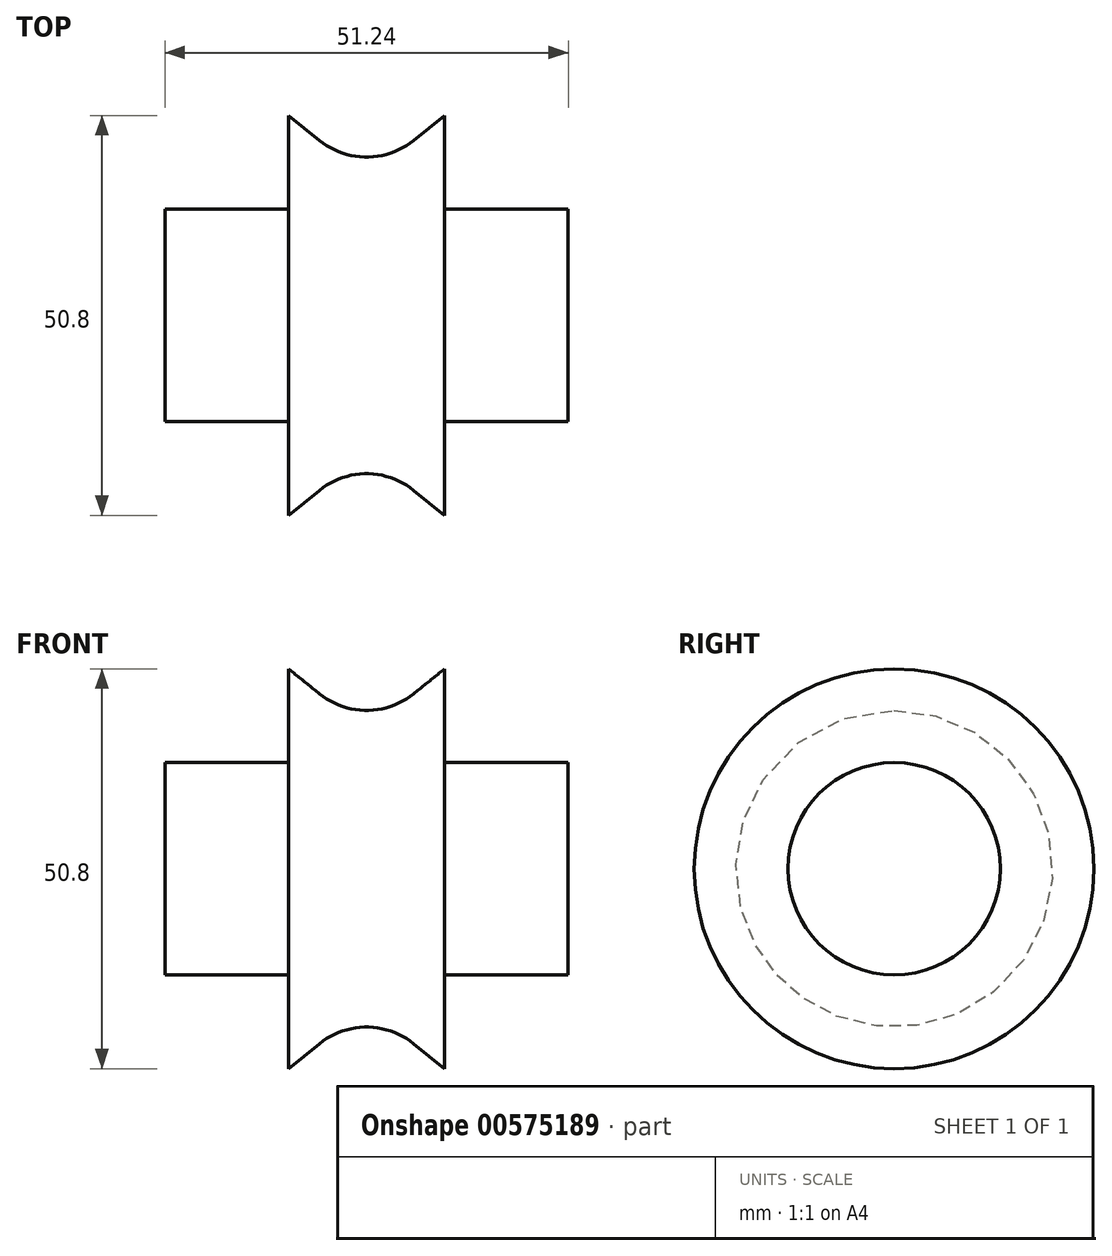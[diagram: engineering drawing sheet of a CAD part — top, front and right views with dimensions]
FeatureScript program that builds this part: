
annotation { "Feature Type Name" : "Feature", "Feature Type Description" : "" }
export const myFeature = defineFeature(function(context is Context, id is Id, definition is map)
    precondition{}
    {
        {
            var Q0;
            Q0=qCreatedBy(makeId("Front.planeOp"),FACE);
            var sketch = newSketch(context, id + "F0", { "sketchPlane" : qUnion([Q0])});
            skLineSegment(sketch, "E0", {"start": v(-25.62, -3.87) * mm, "end": v(-25.62, 9.62) * mm});
            skLineSegment(sketch, "E1", {"start": v(-25.62, 9.62) * mm, "end": v(-9.92, 9.62) * mm});
            skLineSegment(sketch, "E2", {"start": v(-9.92, 9.62) * mm, "end": v(-9.92, 21.53) * mm});
            skLineSegment(sketch, "E3", {"start": v(-9.92, 21.53) * mm, "end": v(-5.98, 18.35) * mm});
            skLineSegment(sketch, "E4", {"start": v(0, 17.59) * mm, "end": v(0, -15.68) * mm, "construction": true});
            skLineSegment(sketch, "E5.MirrorCS", {"start": v(9.92, 21.53) * mm, "end": v(5.98, 18.35) * mm});
            skLineSegment(sketch, "E6.MirrorCS", {"start": v(9.92, 9.62) * mm, "end": v(9.92, 21.53) * mm});
            skLineSegment(sketch, "E7.MirrorCS", {"start": v(25.62, -3.87) * mm, "end": v(25.62, 9.62) * mm});
            skLineSegment(sketch, "E8.MirrorCS", {"start": v(25.62, 9.62) * mm, "end": v(9.92, 9.62) * mm});
            skArc(sketch, "E9", {"start": v(-5.98, 18.35) * mm, "mid": v(0, 16.24) * mm, "end": v(5.98, 18.35) * mm});
            skLineSegment(sketch, "E10", {"start": v(-28.8, 0) * mm, "end": v(29.73, 0) * mm, "construction": true});
            skLineSegment(sketch, "E11", {"start": v(-25.62, -3.87) * mm, "end": v(25.62, -3.87) * mm});
            skSolve(sketch);
        }
        {
            var Q0;
            Q0=makeQuery(id+"F0.imprint","IMPRINT",FACE,{"disambiguationData":[TD([[makeQuery(id+"F0.imprint","IMPRINT",EDGE,{"derivedFrom":sQuery(id+"F0.wireOp",EDGE,"E0")}),-1.0]])]});
            var Q1;
            Q1=sQuery(id+"F0.wireOp",EDGE,"E11");
            revolve(context, id + "F1", {"entities" : qUnion([Q0]), "axis" : qUnion([Q1]), "revolveType" : RevolveType.FULL});
        }
    });
